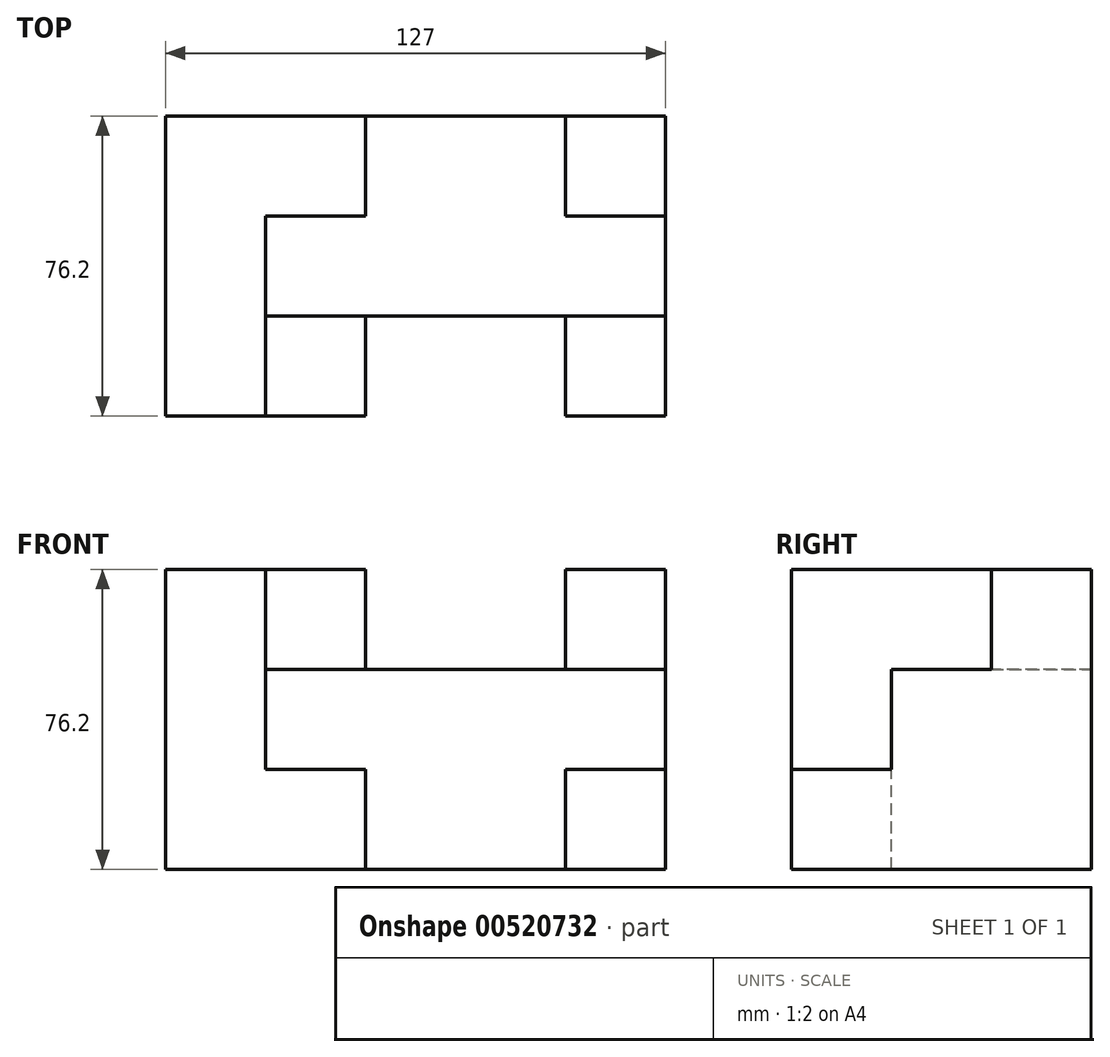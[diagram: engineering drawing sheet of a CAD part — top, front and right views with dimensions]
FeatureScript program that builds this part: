
annotation { "Feature Type Name" : "Feature", "Feature Type Description" : "" }
export const myFeature = defineFeature(function(context is Context, id is Id, definition is map)
    precondition{}
    {
        {
            var Q0;
            Q0=qCreatedBy(makeId("Front.planeOp"),FACE);
            var sketch = newSketch(context, id + "F0", { "sketchPlane" : qUnion([Q0])});
            skLineSegment(sketch, "E0.bottom", {"start": v(-47.66, 10.92) * mm, "end": v(79.34, 10.92) * mm});
            skLineSegment(sketch, "E0.top", {"start": v(-47.66, -65.28) * mm, "end": v(79.34, -65.28) * mm});
            skLineSegment(sketch, "E0.left", {"start": v(-47.66, 10.92) * mm, "end": v(-47.66, -65.28) * mm});
            skLineSegment(sketch, "E0.right", {"start": v(79.34, 10.92) * mm, "end": v(79.34, -65.28) * mm});
            skSolve(sketch);
        }
        {
            var Q0;
            Q0 = qSketchRegion(id + "F0", true);
            extrude(context, id + "F1", {"entities" : qUnion([Q0]), "depth" : 76.2 * mm, "offsetDistance" : 25.4 * mm});
        }
        {
            var Q0;
            Q0=makeQuery(id+"F1.opExtrude","SWEPT_FACE",FACE,{"disambiguationData":[OSD([sQuery(id+"F0.wireOp",EDGE,"E0.bottom")])]});
            var sketch = newSketch(context, id + "F2", { "sketchPlane" : qUnion([Q0])});
            skLineSegment(sketch, "E1.bottom", {"start": v(79.34, 0) * mm, "end": v(53.94, 0) * mm});
            skLineSegment(sketch, "E1.top", {"start": v(79.34, -25.4) * mm, "end": v(53.94, -25.4) * mm});
            skLineSegment(sketch, "E1.left", {"start": v(79.34, 0) * mm, "end": v(79.34, -25.4) * mm});
            skLineSegment(sketch, "E1.right", {"start": v(53.94, 0) * mm, "end": v(53.94, -25.4) * mm});
            skLineSegment(sketch, "E2.bottom", {"start": v(79.34, -76.2) * mm, "end": v(53.94, -76.2) * mm});
            skLineSegment(sketch, "E2.top", {"start": v(79.34, -50.8) * mm, "end": v(53.94, -50.8) * mm});
            skLineSegment(sketch, "E2.left", {"start": v(79.34, -76.2) * mm, "end": v(79.34, -50.8) * mm});
            skLineSegment(sketch, "E2.right", {"start": v(53.94, -76.2) * mm, "end": v(53.94, -50.8) * mm});
            skLineSegment(sketch, "E3", {"start": v(-47.66, -76.2) * mm, "end": v(-22.26, -76.2) * mm});
            skLineSegment(sketch, "E4", {"start": v(-22.26, -76.2) * mm, "end": v(-22.26, -25.39) * mm});
            skLineSegment(sketch, "E5", {"start": v(-22.26, -25.39) * mm, "end": v(3.14, -25.39) * mm});
            skLineSegment(sketch, "E6", {"start": v(3.14, -25.39) * mm, "end": v(3.14, 0) * mm});
            skLineSegment(sketch, "E7.bottom", {"start": v(-22.26, -76.2) * mm, "end": v(3.14, -76.2) * mm});
            skLineSegment(sketch, "E7.top", {"start": v(-22.26, -50.8) * mm, "end": v(3.14, -50.8) * mm});
            skLineSegment(sketch, "E7.left", {"start": v(-22.26, -76.2) * mm, "end": v(-22.26, -50.8) * mm});
            skLineSegment(sketch, "E7.right", {"start": v(3.14, -76.2) * mm, "end": v(3.14, -50.8) * mm});
            skLineSegment(sketch, "E8", {"start": v(3.14, -50.8) * mm, "end": v(53.94, -50.8) * mm});
            skSolve(sketch);
        }
        {
            var Q0;
            {var subQ0=sQuery(id+"F2.wireOp",EDGE,"E2.right");Q0=makeQuery(id+"F2.imprint","IMPRINT",FACE,{"disambiguationData":[TD([[makeQuery(id+"F2.imprint","IMPRINT",EDGE,{"derivedFrom":subQ0}),1.0]])]});}
            extrude(context, id + "F3", {"entities" : qUnion([Q0]), "operationType" : NewBodyOperationType.REMOVE, "oppositeDirection" : true, "depth" : 86.87 * mm, "offsetDistance" : 25.4 * mm});
        }
        {
            var Q0;
            Q0=makeQuery(id+"F2.imprint","IMPRINT",FACE,{"disambiguationData":[TD([[makeQuery(id+"F2.imprint","IMPRINT",EDGE,{"derivedFrom":sQuery(id+"F2.wireOp",EDGE,"E7.bottom")}),1.0]])]});
            var Q1;
            Q1=makeQuery(id+"F2.imprint","IMPRINT",FACE,{"disambiguationData":[TD([[makeQuery(id+"F2.imprint","IMPRINT",EDGE,{"derivedFrom":sQuery(id+"F2.wireOp",EDGE,"E2.bottom")}),1.0]])]});
            extrude(context, id + "F4", {"entities" : qUnion([Q0, Q1]), "operationType" : NewBodyOperationType.REMOVE, "oppositeDirection" : true, "depth" : 50.8 * mm, "offsetDistance" : 25.4 * mm});
        }
        {
            var Q0;
            {var subQ2=sQuery(id+"F2.wireOp",EDGE,"E1.top");Q0=makeQuery(id+"F2.imprint","IMPRINT",FACE,{"disambiguationData":[TD([[makeQuery(id+"F2.imprint","IMPRINT",EDGE,{"derivedFrom":subQ2}),1.0]])]});}
            extrude(context, id + "F5", {"entities" : qUnion([Q0]), "operationType" : NewBodyOperationType.REMOVE, "oppositeDirection" : true, "depth" : 25.4 * mm, "offsetDistance" : 25.4 * mm});
        }
    });
